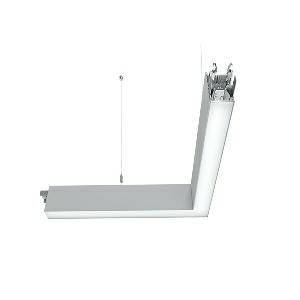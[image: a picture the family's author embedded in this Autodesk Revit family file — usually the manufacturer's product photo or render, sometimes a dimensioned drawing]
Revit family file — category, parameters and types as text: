
# Revit family: dotoo_line_-_dlp_1500_840_d_ll_mid_00807696_63e6
name_source: partatom
category: Lighting Fixtures
units: mm (PartAtom-declared; Revit-internal decimal feet)

## family parameters
Cut with Voids When Loaded = No
Host = Face
Light Source = No
Part Type = Normal
Room Calculation Point = No
Round Connector Dimension = Use Diameter
Shared = No

## types (1)
- DOTOO.line - DLP 1500/840/D/LL MID (1 x LED, 1350 lm, 4000K)
    Apparent Load = 13 VA
    Approval mark = CE
    CIE Flux Codes = 67 91 98 100 100
    Color Rendering = 80-89
    Color Temperature = 4000K
    Control Gear = Electronic ballast
    Default Elevation = 1800 mm
    Description = DLP 1500/840/D|Suspended luminaire|light source: LED|connected load: 220-240 V, 50/60 Hz|Power consumption: approx. 13 W|standby: approx. 0,20|luminous flux: 1350 lm|luminous efficacy: 103 lm/W|light distribution: Direct|direct ratio: approx. 100 %|colour temperature: Cold white, ca. 4000 K|color rendering index (CRI): >= 80|chromaticity tolerance:  3 SDCM|System of protection: IP 40|technology: Continuously dimmable|luminaire body|material: Sectional aluminium|colour: Silver|lamp cover: Acrylic (PMMA), Clear|Fastening: Steel cable 0.3 - 0.7 m|glare control: Prism aperture|luminance(L65): <= 3000 cd/m|unified glare rating(4H 8H): <=  19|special features: DALI Load 1x, TouchDIM - dimming via standard switch, Through-wired, up to 18 m on one mains connection, Flicker-free, Continous light without dark z, 90░ rerouting on the left side, Suitable as emergency lighting, Mechanical and electrical connection of the individual modules without tools|
    Frequency = 50 Hz
    Height = 110 mm
    Lamp = 1 x LED
    Lamp Light Flux = 1350 lm
    Lamp count = 1
    Length = 600 mm
    Luminous efficacy = 104 lm/W
    Manufacturer = Waldmann
    ModVariant = No
    Model = 00807696
    Mounting Place = Ceiling
    Mounting Type = Pendant
    Number of Poles = 1
    OnlyDefault = Yes
    Power Factor = 1
    Product Name = DOTOO.line - DLP 1500/840/D/LL MID
    Product group = Suspended luminaire
    ProductGroupID = 9
    Protection Class = Protection class I
    Protection Degree = IP 40
    RLX_Detail_Level = 1
    RLX_Emergency_Light_Flux = 0 lm
    RLX_Emergency_Type = 0
    RLX_Emergency_Type_DB = No
    RlxData = <blob elided: 21873 chars, md5=91a4f1ea>
    Socket = socket
    Standby Power = 0 W
    System Light Flux = 1350 lm
    System Power = 13 W
    Type Comments = Product without accessories
    Type Image = ilp_dlp_ll_si.jpg
    URL = http://relux.com
    VarID = ---
    Voltage = 230 V
    Voltage Range = 220-240 V
    Weight = 0.00 kg
    Width = 600 mm

## geometry (parser evidence)
native form markers: Blend x4, Sweep x13
no freeform markers — native parametric forms only
